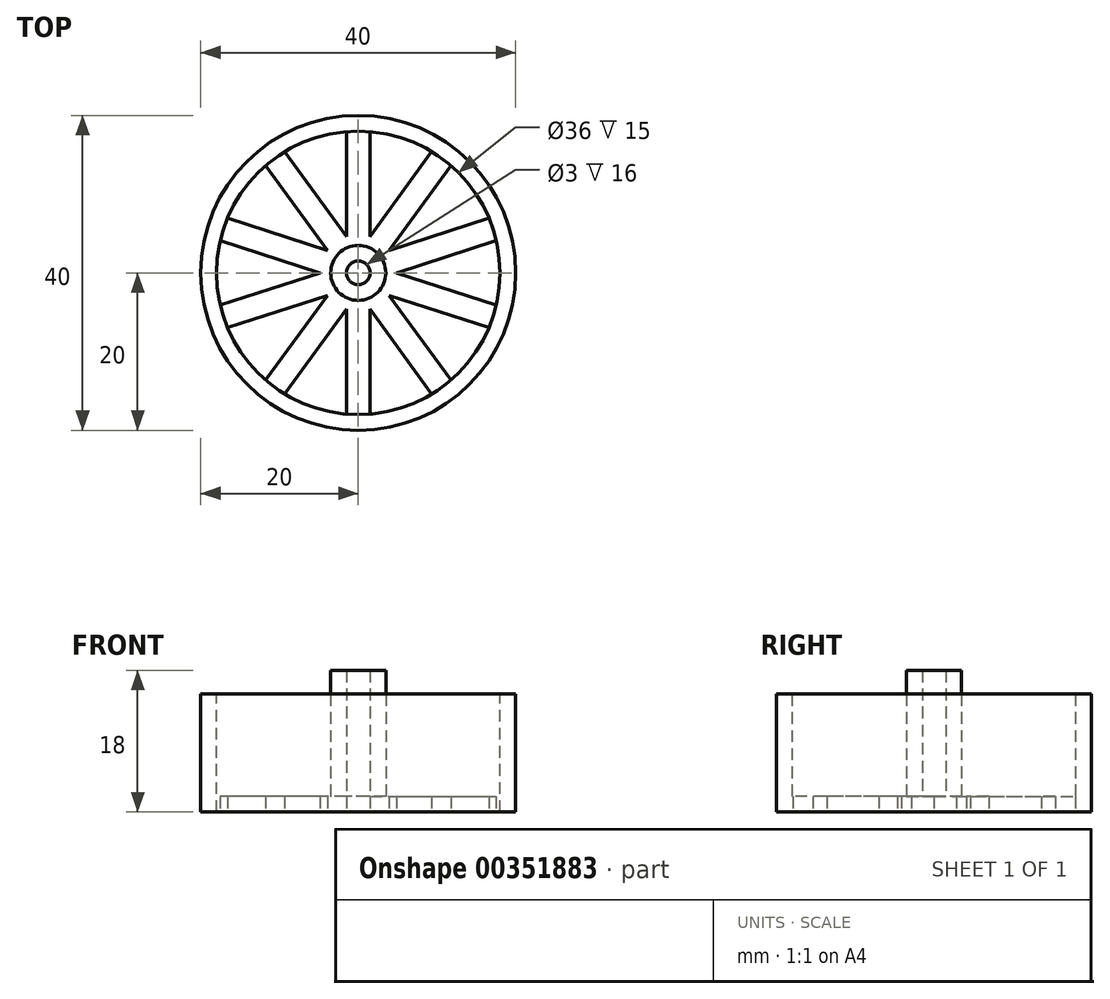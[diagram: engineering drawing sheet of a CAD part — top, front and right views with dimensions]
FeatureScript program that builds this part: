
annotation { "Feature Type Name" : "Feature", "Feature Type Description" : "" }
export const myFeature = defineFeature(function(context is Context, id is Id, definition is map)
    precondition{}
    {
        {
            var Q0;
            Q0=qCreatedBy(makeId("Top.planeOp"),FACE);
            var sketch = newSketch(context, id + "F0", { "sketchPlane" : qUnion([Q0])});
            skCircle(sketch, "E0", {"center": v(0, 0) * mm, "radius": 20 * mm});
            skSolve(sketch);
        }
        {
            var Q0;
            Q0=makeQuery(id+"F0.imprint","IMPRINT",FACE,{"disambiguationData":[TD([[makeQuery(id+"F0.imprint","IMPRINT",EDGE,{"derivedFrom":sQuery(id+"F0.wireOp",EDGE,"E0")}),1.0]])]});
            extrude(context, id + "F1", {"entities" : qUnion([Q0]), "depth" : 15 * mm});
        }
        {
            var Q0;
            Q0=makeQuery(id+"F1.opExtrude","CAP_FACE",FACE,{"disambiguationData":[OSD([sQuery(id+"F0.wireOp",EDGE,"E0")])],"isStart":false});
            var sketch = newSketch(context, id + "F2", { "sketchPlane" : qUnion([Q0])});
            skCircle(sketch, "E1", {"center": v(0, 0) * mm, "radius": 18 * mm});
            skSolve(sketch);
        }
        {
            var Q0;
            Q0=makeQuery(id+"F2.imprint","IMPRINT",FACE,{"disambiguationData":[TD([[makeQuery(id+"F2.imprint","IMPRINT",EDGE,{"derivedFrom":sQuery(id+"F2.wireOp",EDGE,"E1")}),1.0]])]});
            extrude(context, id + "F3", {"entities" : qUnion([Q0]), "operationType" : NewBodyOperationType.REMOVE, "oppositeDirection" : true, "depth" : 13 * mm});
        }
        {
            var Q0;
            Q0=makeQuery(id+"F3.boolean.opBoolean","COPY",FACE,{"derivedFrom":makeQuery(id+"F3.opExtrude","CAP_FACE",FACE,{"disambiguationData":[OSD([sQuery(id+"F2.wireOp",EDGE,"E1")])],"isStart":false})});
            var sketch = newSketch(context, id + "F4", { "sketchPlane" : qUnion([Q0])});
            skSolve(sketch);
        }
        {
            var Q0;
            Q0=makeQuery(id+"F4.imprint","IMPRINT",FACE,{"disambiguationData":[TD([[makeQuery(id+"F4.imprint","IMPRINT",EDGE,{"derivedFrom":makeQuery(id+"F3.boolean.opBoolean","COPY",EDGE,{"derivedFrom":makeQuery(id+"F3.opExtrude","CAP_EDGE",EDGE,{"disambiguationData":[OSD([sQuery(id+"F2.wireOp",EDGE,"E1")])],"isStart":false})})}),1.0]])]});
            var sketch = newSketch(context, id + "F5", { "sketchPlane" : qUnion([Q0])});
            skCircle(sketch, "E2", {"center": v(0, 0) * mm, "radius": 1.5 * mm});
            skCircle(sketch, "E3", {"center": v(0, 0) * mm, "radius": 3.5 * mm});
            skSolve(sketch);
        }
        {
            var Q0;
            Q0=makeQuery(id+"F5.imprint","IMPRINT",FACE,{"disambiguationData":[TD([[makeQuery(id+"F5.imprint","IMPRINT",EDGE,{"derivedFrom":sQuery(id+"F5.wireOp",EDGE,"E2")}),-1.0]])]});
            extrude(context, id + "F6", {"entities" : qUnion([Q0]), "operationType" : NewBodyOperationType.ADD, "depth" : 16 * mm});
        }
        {
            var Q0;
            Q0=qCreatedBy(makeId("Top.planeOp"),FACE);
            var sketch = newSketch(context, id + "F7", { "sketchPlane" : qUnion([Q0])});
            skLineSegment(sketch, "E4.0", {"start": v(1.5, 0) * mm, "end": v(1.5, 18.25) * mm});
            skLineSegment(sketch, "E5.MirrorCS", {"start": v(-1.5, 0) * mm, "end": v(-1.5, 18.25) * mm});
            skLineSegment(sketch, "E6.1.0", {"start": v(1.21, 0.88) * mm, "end": v(-9.51, 15.65) * mm});
            skLineSegment(sketch, "E6.1.1", {"start": v(-1.21, -0.88) * mm, "end": v(-11.94, 13.88) * mm});
            skLineSegment(sketch, "E6.2.0", {"start": v(0.46, 1.43) * mm, "end": v(-16.9, 7.07) * mm});
            skLineSegment(sketch, "E6.2.1", {"start": v(-0.46, -1.43) * mm, "end": v(-17.82, 4.21) * mm});
            skLineSegment(sketch, "E6.3.0", {"start": v(-0.46, 1.43) * mm, "end": v(-17.82, -4.21) * mm});
            skLineSegment(sketch, "E6.3.1", {"start": v(0.46, -1.43) * mm, "end": v(-16.9, -7.07) * mm});
            skLineSegment(sketch, "E6.4.0", {"start": v(-1.21, 0.88) * mm, "end": v(-11.94, -13.88) * mm});
            skLineSegment(sketch, "E6.4.1", {"start": v(1.21, -0.88) * mm, "end": v(-9.51, -15.65) * mm});
            skLineSegment(sketch, "E6.5.0", {"start": v(-1.5, 0) * mm, "end": v(-1.5, -18.25) * mm});
            skLineSegment(sketch, "E6.5.1", {"start": v(1.5, 0) * mm, "end": v(1.5, -18.25) * mm});
            skLineSegment(sketch, "E6.6.0", {"start": v(-1.21, -0.88) * mm, "end": v(9.51, -15.65) * mm});
            skLineSegment(sketch, "E6.6.1", {"start": v(1.21, 0.88) * mm, "end": v(11.94, -13.88) * mm});
            skLineSegment(sketch, "E6.7.0", {"start": v(-0.46, -1.43) * mm, "end": v(16.9, -7.07) * mm});
            skLineSegment(sketch, "E6.7.1", {"start": v(0.46, 1.43) * mm, "end": v(17.82, -4.21) * mm});
            skLineSegment(sketch, "E6.8.0", {"start": v(0.46, -1.43) * mm, "end": v(17.82, 4.21) * mm});
            skLineSegment(sketch, "E6.8.1", {"start": v(-0.46, 1.43) * mm, "end": v(16.9, 7.07) * mm});
            skLineSegment(sketch, "E6.9.0", {"start": v(1.21, -0.88) * mm, "end": v(11.94, 13.88) * mm});
            skLineSegment(sketch, "E6.9.1", {"start": v(-1.21, 0.88) * mm, "end": v(9.51, 15.65) * mm});
            skPoint(sketch, "E6.center", {"position": v(0, 0) * mm});
            skCircle(sketch, "E7", {"center": v(0, 0) * mm, "radius": 18 * mm});
            skSolve(sketch);
        }
        {
            var Q0;
            {var subQ0=sQuery(id+"F7.wireOp",EDGE,"E7");var subQ1=sQuery(id+"F7.wireOp",EDGE,"E6.4.1");var subQ2=makeQuery(id+"F7.imprint","INTERSECT",VERTEX,{"derivedFrom":[subQ1,subQ0]});Q0=makeQuery(id+"F7.imprint","IMPRINT",FACE,{"disambiguationData":[TD([[makeQuery(id+"F7.imprint","IMPRINT",EDGE,{"disambiguationData":[TD([[subQ2,1.0]])],"derivedFrom":subQ1}),1.0]])]});}
            var Q1;
            {var subQ0=sQuery(id+"F7.wireOp",EDGE,"E7");var subQ1=sQuery(id+"F7.wireOp",EDGE,"E6.5.1");var subQ2=makeQuery(id+"F7.imprint","INTERSECT",VERTEX,{"derivedFrom":[subQ1,subQ0]});Q1=makeQuery(id+"F7.imprint","IMPRINT",FACE,{"disambiguationData":[TD([[makeQuery(id+"F7.imprint","IMPRINT",EDGE,{"disambiguationData":[TD([[subQ2,1.0]])],"derivedFrom":subQ1}),1.0]])]});}
            var Q2;
            {var subQ0=sQuery(id+"F7.wireOp",EDGE,"E7");var subQ1=sQuery(id+"F7.wireOp",EDGE,"E6.6.1");var subQ2=makeQuery(id+"F7.imprint","INTERSECT",VERTEX,{"derivedFrom":[subQ1,subQ0]});Q2=makeQuery(id+"F7.imprint","IMPRINT",FACE,{"disambiguationData":[TD([[makeQuery(id+"F7.imprint","IMPRINT",EDGE,{"disambiguationData":[TD([[subQ2,1.0]])],"derivedFrom":subQ1}),1.0]])]});}
            var Q3;
            {var subQ0=sQuery(id+"F7.wireOp",EDGE,"E7");var subQ1=sQuery(id+"F7.wireOp",EDGE,"E6.7.1");var subQ2=makeQuery(id+"F7.imprint","INTERSECT",VERTEX,{"derivedFrom":[subQ1,subQ0]});Q3=makeQuery(id+"F7.imprint","IMPRINT",FACE,{"disambiguationData":[TD([[makeQuery(id+"F7.imprint","IMPRINT",EDGE,{"disambiguationData":[TD([[subQ2,1.0]])],"derivedFrom":subQ1}),1.0]])]});}
            var Q4;
            {var subQ0=sQuery(id+"F7.wireOp",EDGE,"E7");var subQ1=sQuery(id+"F7.wireOp",EDGE,"E6.8.1");var subQ2=makeQuery(id+"F7.imprint","INTERSECT",VERTEX,{"derivedFrom":[subQ1,subQ0]});Q4=makeQuery(id+"F7.imprint","IMPRINT",FACE,{"disambiguationData":[TD([[makeQuery(id+"F7.imprint","IMPRINT",EDGE,{"disambiguationData":[TD([[subQ2,1.0]])],"derivedFrom":subQ1}),1.0]])]});}
            var Q5;
            {var subQ0=sQuery(id+"F7.wireOp",EDGE,"E7");var subQ1=sQuery(id+"F7.wireOp",EDGE,"E4.0");var subQ2=makeQuery(id+"F7.imprint","INTERSECT",VERTEX,{"derivedFrom":[subQ1,subQ0]});Q5=makeQuery(id+"F7.imprint","IMPRINT",FACE,{"disambiguationData":[TD([[makeQuery(id+"F7.imprint","IMPRINT",EDGE,{"disambiguationData":[TD([[subQ2,1.0]])],"derivedFrom":subQ1}),-1.0]])]});}
            var Q6;
            {var subQ0=sQuery(id+"F7.wireOp",EDGE,"E7");var subQ1=sQuery(id+"F7.wireOp",EDGE,"E5.MirrorCS");var subQ2=makeQuery(id+"F7.imprint","INTERSECT",VERTEX,{"derivedFrom":[subQ1,subQ0]});Q6=makeQuery(id+"F7.imprint","IMPRINT",FACE,{"disambiguationData":[TD([[makeQuery(id+"F7.imprint","IMPRINT",EDGE,{"disambiguationData":[TD([[subQ2,1.0]])],"derivedFrom":subQ1}),1.0]])]});}
            var Q7;
            {var subQ0=sQuery(id+"F7.wireOp",EDGE,"E7");var subQ1=sQuery(id+"F7.wireOp",EDGE,"E6.1.1");var subQ2=makeQuery(id+"F7.imprint","INTERSECT",VERTEX,{"derivedFrom":[subQ1,subQ0]});Q7=makeQuery(id+"F7.imprint","IMPRINT",FACE,{"disambiguationData":[TD([[makeQuery(id+"F7.imprint","IMPRINT",EDGE,{"disambiguationData":[TD([[subQ2,1.0]])],"derivedFrom":subQ1}),1.0]])]});}
            var Q8;
            {var subQ0=sQuery(id+"F7.wireOp",EDGE,"E7");var subQ1=sQuery(id+"F7.wireOp",EDGE,"E6.2.1");var subQ2=makeQuery(id+"F7.imprint","INTERSECT",VERTEX,{"derivedFrom":[subQ1,subQ0]});Q8=makeQuery(id+"F7.imprint","IMPRINT",FACE,{"disambiguationData":[TD([[makeQuery(id+"F7.imprint","IMPRINT",EDGE,{"disambiguationData":[TD([[subQ2,1.0]])],"derivedFrom":subQ1}),1.0]])]});}
            var Q9;
            {var subQ0=sQuery(id+"F7.wireOp",EDGE,"E7");var subQ1=sQuery(id+"F7.wireOp",EDGE,"E6.3.1");var subQ2=makeQuery(id+"F7.imprint","INTERSECT",VERTEX,{"derivedFrom":[subQ1,subQ0]});Q9=makeQuery(id+"F7.imprint","IMPRINT",FACE,{"disambiguationData":[TD([[makeQuery(id+"F7.imprint","IMPRINT",EDGE,{"disambiguationData":[TD([[subQ2,1.0]])],"derivedFrom":subQ1}),1.0]])]});}
            extrude(context, id + "F8", {"entities" : qUnion([Q0, Q1, Q2, Q3, Q4, Q5, Q6, Q7, Q8, Q9]), "operationType" : NewBodyOperationType.REMOVE, "depth" : 2 * mm});
        }
    });
